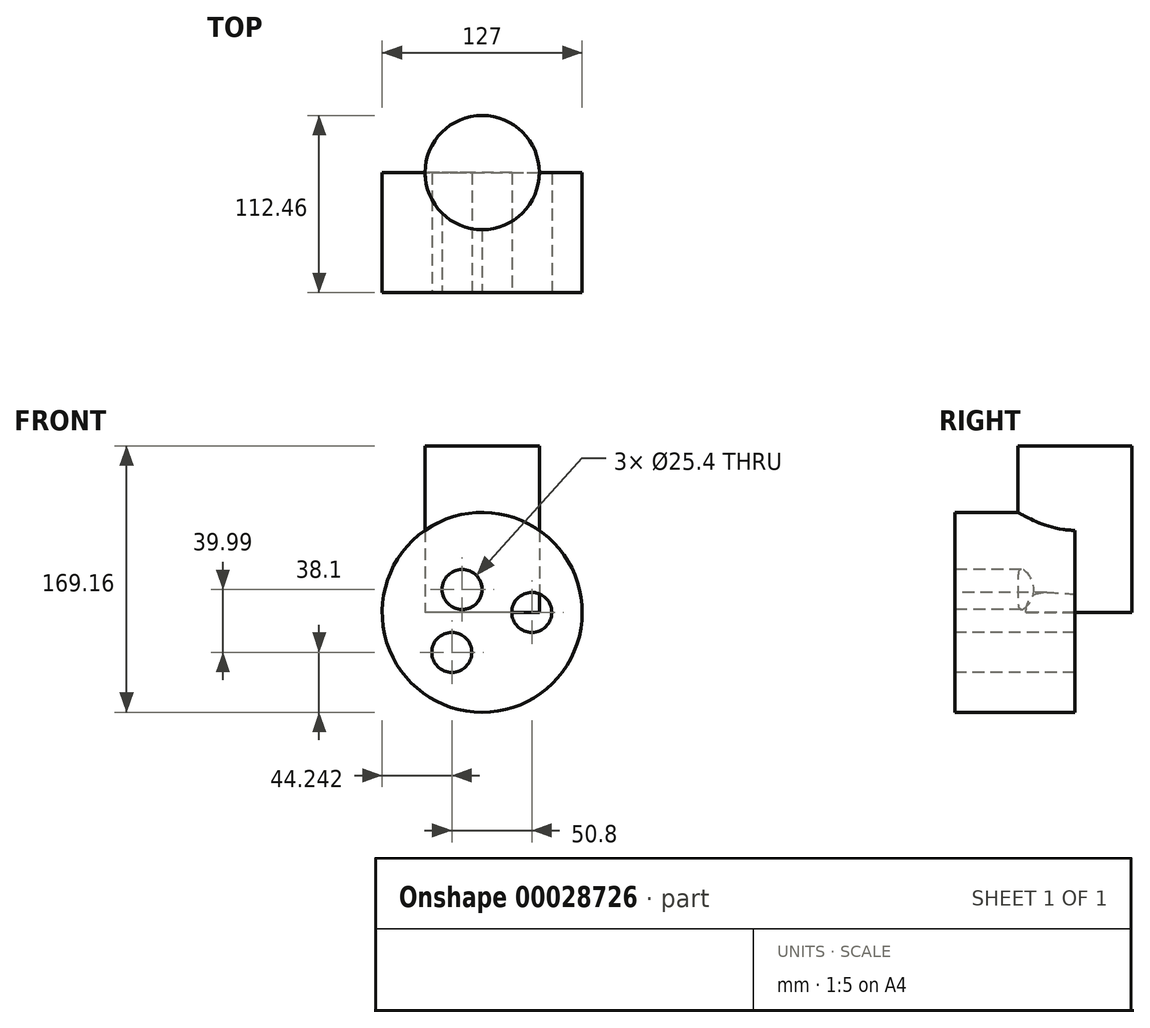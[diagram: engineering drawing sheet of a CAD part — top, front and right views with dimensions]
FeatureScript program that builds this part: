
annotation { "Feature Type Name" : "Feature", "Feature Type Description" : "" }
export const myFeature = defineFeature(function(context is Context, id is Id, definition is map)
    precondition{}
    {
        {
            var Q0;
            Q0=qCreatedBy(makeId("Front.planeOp"),FACE);
            var sketch = newSketch(context, id + "F0", { "sketchPlane" : qUnion([Q0])});
            skCircle(sketch, "E0", {"center": v(0, 0) * mm, "radius": 63.5 * mm});
            skSolve(sketch);
        }
        {
            var Q0;
            Q0=makeQuery(id+"F0.imprint","IMPRINT",FACE,{"disambiguationData":[TD([[makeQuery(id+"F0.imprint","IMPRINT",EDGE,{"derivedFrom":sQuery(id+"F0.wireOp",EDGE,"E0")}),1.0]])]});
            extrude(context, id + "F1", {"entities" : qUnion([Q0]), "depth" : 76.2 * mm});
        }
        {
            var Q0;
            Q0=makeQuery(id+"F1.opExtrude","CAP_FACE",FACE,{"disambiguationData":[OSD([sQuery(id+"F0.wireOp",EDGE,"E0")])],"isStart":false});
            var sketch = newSketch(context, id + "F2", { "sketchPlane" : qUnion([Q0])});
            skPoint(sketch, "E1", {"position": v(0, 0) * mm});
            skPoint(sketch, "E2", {"position": v(31.54, 0) * mm});
            skPoint(sketch, "E3", {"position": v(-12.7, 14.59) * mm});
            skPoint(sketch, "E4", {"position": v(-19.26, -25.4) * mm});
            skSolve(sketch);
        }
        {
            var Q0;
            Q0=sQuery(id+"F2.wireOp",VERTEX,"E4");
            var Q1;
            Q1=sQuery(id+"F2.wireOp",VERTEX,"E3");
            var Q2;
            Q2=sQuery(id+"F2.wireOp",VERTEX,"E2");
            var Q3;
            Q3=makeQuery(id+"F1.opExtrude","SWEPT_BODY",BODY,{"disambiguationData":[OSD([sQuery(id+"F0.wireOp",EDGE,"E0")])]});
            hole(context, id + "F3", {"style" : HoleStyle.SIMPLE, "holeDiameter" : 25.4 * mm, "endStyle" : HoleEndStyle.THROUGH, "locations" : qUnion([Q0, Q1, Q2]), "scope" : qUnion([Q3])});
        }
        {
            var Q0;
            Q0=qCreatedBy(makeId("Top.planeOp"),FACE);
            var sketch = newSketch(context, id + "F4", { "sketchPlane" : qUnion([Q0])});
            skCircle(sketch, "E5", {"center": v(0, 0) * mm, "radius": 36.26 * mm});
            skSolve(sketch);
        }
        {
            var Q0;
            Q0 = qSketchRegion(id + "F4", true);
            extrude(context, id + "F5", {"entities" : qUnion([Q0]), "operationType" : NewBodyOperationType.ADD, "depth" : 105.66 * mm, "offsetDistance" : 25.4 * mm});
        }
    });
